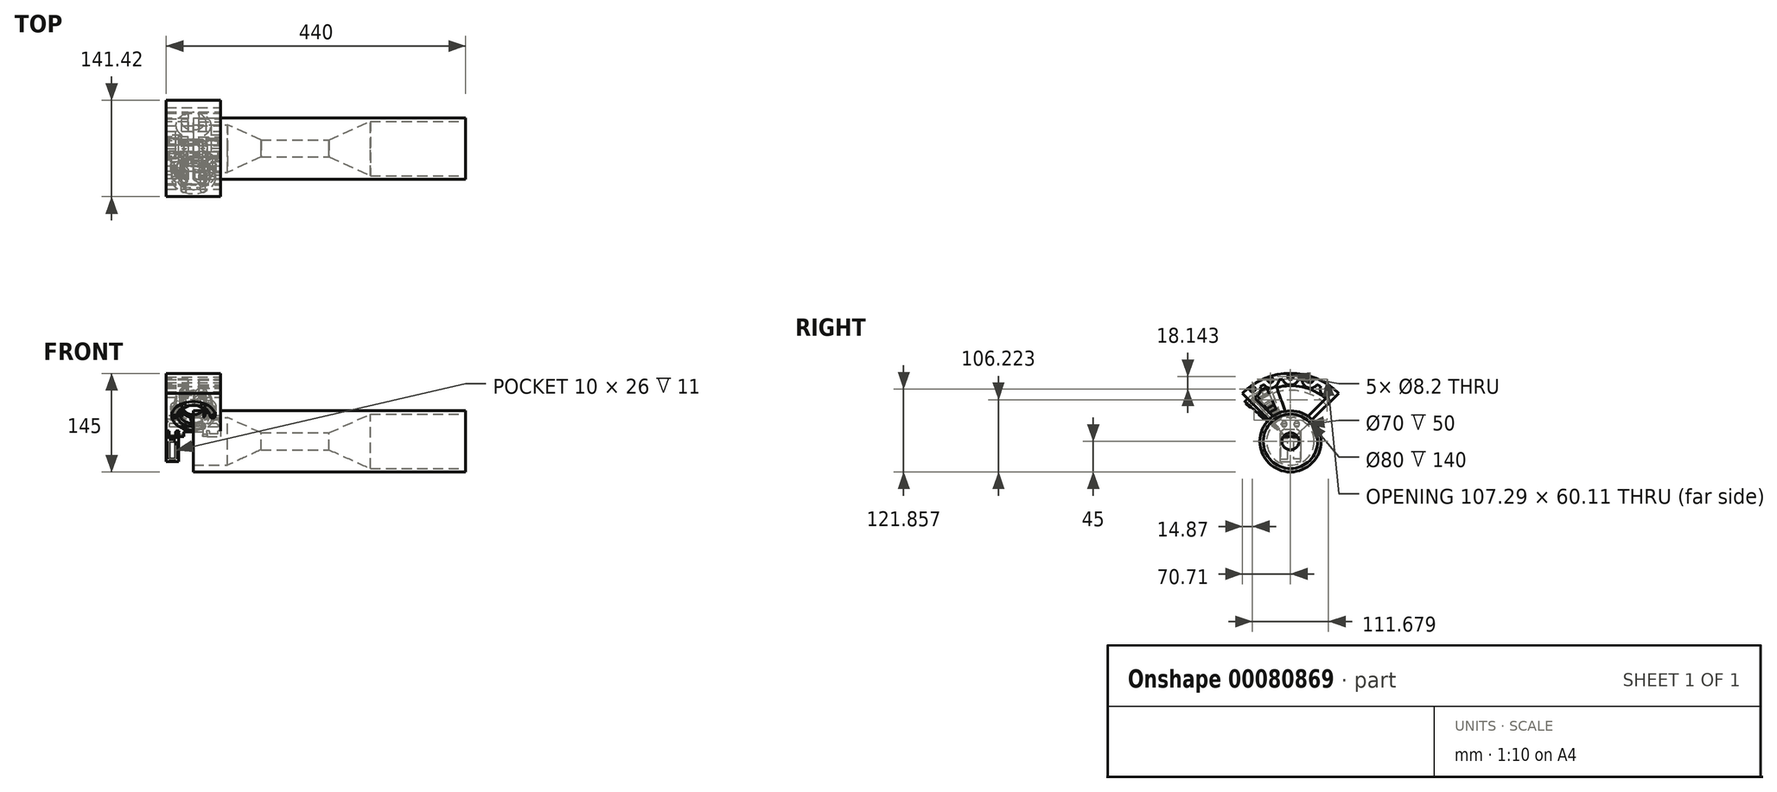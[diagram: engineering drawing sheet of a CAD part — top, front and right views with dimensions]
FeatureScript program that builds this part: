
annotation { "Feature Type Name" : "Feature", "Feature Type Description" : "" }
export const myFeature = defineFeature(function(context is Context, id is Id, definition is map)
    precondition{}
    {
        {
            var Q0;
            Q0=qCreatedBy(makeId("Front.planeOp"),FACE);
            var sketch = newSketch(context, id + "F0", { "sketchPlane" : qUnion([Q0])});
            skLineSegment(sketch, "E0.bottom", {"start": v(-40, 30) * mm, "end": v(40, 30) * mm});
            skLineSegment(sketch, "E0.top", {"start": v(-40, -30) * mm, "end": v(40, -30) * mm});
            skLineSegment(sketch, "E0.left", {"start": v(-40, 30) * mm, "end": v(-40, -30) * mm});
            skLineSegment(sketch, "E0.right", {"start": v(40, 30) * mm, "end": v(40, -30) * mm});
            skPoint(sketch, "E0.middle", {"position": v(0, 0) * mm});
            skLineSegment(sketch, "E1", {"start": v(-22, -30) * mm, "end": v(-22, 18) * mm});
            skLineSegment(sketch, "E2", {"start": v(-22, 18) * mm, "end": v(20, 18) * mm});
            skLineSegment(sketch, "E3", {"start": v(20, 18) * mm, "end": v(20, 7) * mm});
            skLineSegment(sketch, "E4", {"start": v(20, 7) * mm, "end": v(40, 7) * mm});
            skSolve(sketch);
        }
        {
            var Q0;
            {var subQ1=sQuery(id+"F0.wireOp",EDGE,"E0.bottom");Q0=makeQuery(id+"F0.imprint","IMPRINT",FACE,{"disambiguationData":[TD([[makeQuery(id+"F0.imprint","IMPRINT",EDGE,{"derivedFrom":subQ1}),-1.0]])]});}
            extrude(context, id + "F1", {"entities" : qUnion([Q0]), "depth" : 15 * mm});
        }
        {
            var Q0;
            Q0=makeQuery(id+"F1.opExtrude","SWEPT_EDGE",EDGE,{"disambiguationData":[OSD([sQuery(id+"F0.wireOp",EDGE,"E1"),sQuery(id+"F0.wireOp",EDGE,"E2")])]});
            var Q1;
            Q1=makeQuery(id+"F1.opExtrude","SWEPT_EDGE",EDGE,{"disambiguationData":[OSD([sQuery(id+"F0.wireOp",EDGE,"E2"),sQuery(id+"F0.wireOp",EDGE,"E3")])]});
            var Q2;
            Q2=makeQuery(id+"F1.opExtrude","SWEPT_EDGE",EDGE,{"disambiguationData":[OSD([sQuery(id+"F0.wireOp",EDGE,"E0.bottom"),sQuery(id+"F0.wireOp",EDGE,"E0.right")])]});
            var Q3;
            Q3=makeQuery(id+"F1.opExtrude","SWEPT_EDGE",EDGE,{"disambiguationData":[OSD([sQuery(id+"F0.wireOp",EDGE,"E0.bottom"),sQuery(id+"F0.wireOp",EDGE,"E0.left")])]});
            fillet(context, id + "F2", {"entities" : qUnion([Q0, Q1, Q2, Q3]), "radius" : 6 * mm, "tangentPropagation" : true, "allowEdgeOverflow" : false});
        }
        {
            var Q0;
            Q0=makeQuery(id+"F1.opExtrude","CAP_FACE",FACE,{"disambiguationData":[OSD([sQuery(id+"F0.wireOp",EDGE,"E0.bottom"),sQuery(id+"F0.wireOp",EDGE,"E0.top"),sQuery(id+"F0.wireOp",EDGE,"E0.left"),sQuery(id+"F0.wireOp",EDGE,"E0.right"),sQuery(id+"F0.wireOp",EDGE,"E1"),sQuery(id+"F0.wireOp",EDGE,"E2"),sQuery(id+"F0.wireOp",EDGE,"E3"),sQuery(id+"F0.wireOp",EDGE,"E4")])],"isStart":false});
            shell(context, id + "F3", {"entities" : qUnion([Q0]), "thickness" : 4 * mm});
        }
        {
            var Q0;
            Q0=qCreatedBy(makeId("Front.planeOp"),FACE);
            var sketch = newSketch(context, id + "F4", { "sketchPlane" : qUnion([Q0])});
            skLineSegment(sketch, "E5.bottom", {"start": v(-15, 18) * mm, "end": v(-11, 18) * mm});
            skLineSegment(sketch, "E5.top", {"start": v(-15, 30) * mm, "end": v(-11, 30) * mm});
            skLineSegment(sketch, "E5.left", {"start": v(-15, 18) * mm, "end": v(-15, 30) * mm});
            skLineSegment(sketch, "E5.right", {"start": v(-11, 18) * mm, "end": v(-11, 30) * mm});
            skLineSegment(sketch, "E6.bottom", {"start": v(13, 18) * mm, "end": v(9, 18) * mm});
            skLineSegment(sketch, "E6.top", {"start": v(13, 30) * mm, "end": v(9, 30) * mm});
            skLineSegment(sketch, "E6.left", {"start": v(13, 18) * mm, "end": v(13, 30) * mm});
            skLineSegment(sketch, "E6.right", {"start": v(9, 18) * mm, "end": v(9, 30) * mm});
            skLineSegment(sketch, "E7.bottom", {"start": v(-22, 4) * mm, "end": v(-40, 4) * mm});
            skLineSegment(sketch, "E7.top", {"start": v(-22, 0) * mm, "end": v(-40, 0) * mm});
            skLineSegment(sketch, "E7.left", {"start": v(-22, 4) * mm, "end": v(-22, 0) * mm});
            skLineSegment(sketch, "E7.right", {"start": v(-40, 4) * mm, "end": v(-40, 0) * mm});
            skSolve(sketch);
        }
        {
            var Q0;
            Q0 = qSketchRegion(id + "F4", true);
            var Q1;
            Q1=makeQuery(id+"F1.opExtrude","CAP_FACE",FACE,{"disambiguationData":[OSD([sQuery(id+"F0.wireOp",EDGE,"E0.bottom"),sQuery(id+"F0.wireOp",EDGE,"E0.top"),sQuery(id+"F0.wireOp",EDGE,"E0.left"),sQuery(id+"F0.wireOp",EDGE,"E0.right"),sQuery(id+"F0.wireOp",EDGE,"E1"),sQuery(id+"F0.wireOp",EDGE,"E2"),sQuery(id+"F0.wireOp",EDGE,"E3"),sQuery(id+"F0.wireOp",EDGE,"E4")])],"isStart":false});
            extrude(context, id + "F5", {"entities" : qUnion([Q0]), "operationType" : NewBodyOperationType.ADD, "endBound" : BoundingType.UP_TO_SURFACE, "endBoundEntityFace" : qUnion([Q1]), "depth" : 25 * mm});
        }
        {
            var Q0;
            Q0=qCreatedBy(makeId("Front.planeOp"),FACE);
            var sketch = newSketch(context, id + "F6", { "sketchPlane" : qUnion([Q0])});
            skCircle(sketch, "E8", {"center": v(0, 57) * mm, "radius": 18 * mm});
            skLineSegment(sketch, "E9", {"start": v(0, 57) * mm, "end": v(0, 75) * mm, "construction": true});
            skLineSegment(sketch, "E10", {"start": v(0, 75) * mm, "end": v(0, 100) * mm});
            skLineSegment(sketch, "E11", {"start": v(0, 100) * mm, "end": v(-40, 100) * mm});
            skLineSegment(sketch, "E12", {"start": v(-40, 100) * mm, "end": v(-40, 10) * mm});
            skLineSegment(sketch, "E13", {"start": v(-40, 10) * mm, "end": v(0, 10) * mm});
            skLineSegment(sketch, "E14", {"start": v(0, 10) * mm, "end": v(0, 39) * mm});
            skCircle(sketch, "E15", {"center": v(0, 57) * mm, "radius": 21 * mm});
            skLineSegment(sketch, "E16", {"start": v(0, 57) * mm, "end": v(0, 78) * mm, "construction": true});
            skLineSegment(sketch, "E17", {"start": v(-14, 20) * mm, "end": v(-14, 10) * mm});
            skLineSegment(sketch, "E18", {"start": v(0, 100) * mm, "end": v(40, 100) * mm});
            skLineSegment(sketch, "E19", {"start": v(40, 100) * mm, "end": v(40, 10) * mm});
            skLineSegment(sketch, "E20", {"start": v(40, 10) * mm, "end": v(0, 10) * mm});
            skLineSegment(sketch, "E21", {"start": v(14, 20) * mm, "end": v(14, 10) * mm});
            skLineSegment(sketch, "E22", {"start": v(-14, 20) * mm, "end": v(0, 20) * mm});
            skLineSegment(sketch, "E23", {"start": v(0, 20) * mm, "end": v(14, 20) * mm});
            skLineSegment(sketch, "E24", {"start": v(-73.82, 0) * mm, "end": v(0, 0) * mm, "construction": true});
            skLineSegment(sketch, "E25", {"start": v(-7, 20) * mm, "end": v(-7, 69.12) * mm});
            skLineSegment(sketch, "E26", {"start": v(7, 69.12) * mm, "end": v(7, 20) * mm});
            skArc(sketch, "E27", {"start": v(-7, 44.88) * mm, "mid": v(0, 43) * mm, "end": v(7, 44.88) * mm});
            skArc(sketch, "E28.trimOffspring", {"start": v(7, 69.12) * mm, "mid": v(0, 71) * mm, "end": v(-7, 69.12) * mm});
            skSolve(sketch);
        }
        {
            var Q0;
            Q0=qCreatedBy(makeId("Front.planeOp"),FACE);
            var sketch = newSketch(context, id + "F7", { "sketchPlane" : qUnion([Q0])});
            skCircle(sketch, "E29", {"center": v(0, 57) * mm, "radius": 17.5 * mm});
            skFitSpline(sketch, "E30", {"points": [v(30.32, 90.11) * mm, v(16.42, 89.95) * mm, v(3.9, 90.3) * mm, v(-9.37, 84.06) * mm, v(-14.84, 66.27) * mm], "startDerivative": vector(-71.71, -0.04) * mm, "endDerivative": vector(12.52, -60.5) * mm});
            skLineSegment(sketch, "E31", {"start": v(30.32, 90.11) * mm, "end": v(30.32, 54.44) * mm});
            skFitSpline(sketch, "E32", {"points": [v(30.32, 84.61) * mm, v(15.77, 85.1) * mm, v(3.67, 86.27) * mm, v(-7.6, 81.73) * mm, v(-12.16, 69.59) * mm], "startDerivative": vector(-60.22, -2.48) * mm, "endDerivative": vector(5.72, -55.41) * mm});
            skLineSegment(sketch, "E33", {"start": v(-14.84, 66.27) * mm, "end": v(0, 57) * mm});
            skLineSegment(sketch, "E34", {"start": v(-12.16, 69.59) * mm, "end": v(0, 57) * mm});
            skLineSegment(sketch, "E35", {"start": v(0, 57) * mm, "end": v(12.68, 57) * mm, "construction": true});
            skLineSegment(sketch, "E36", {"start": v(-9.27, 71.84) * mm, "end": v(0, 57) * mm});
            skLineSegment(sketch, "E37", {"start": v(-5.99, 73.44) * mm, "end": v(0, 57) * mm});
            skFitSpline(sketch, "E38", {"points": [v(-9.27, 71.84) * mm, v(-6.14, 79.83) * mm, v(3.5, 83.27) * mm, v(15.33, 81.84) * mm, v(30.32, 79.91) * mm], "startDerivative": vector(-7.84, 49.59) * mm, "endDerivative": vector(53.8, -1.16) * mm});
            skFitSpline(sketch, "E39", {"points": [v(-5.99, 73.44) * mm, v(-4.56, 77.76) * mm, v(3.32, 80.07) * mm, v(14.76, 77.58) * mm, v(30.32, 74.41) * mm], "startDerivative": vector(-8.8, 35.89) * mm, "endDerivative": vector(51.1, -3.45) * mm});
            skLineSegment(sketch, "E40", {"start": v(-9.37, 84.06) * mm, "end": v(-4.56, 77.76) * mm, "construction": true});
            skLineSegment(sketch, "E41", {"start": v(3.9, 90.3) * mm, "end": v(3.32, 80.07) * mm, "construction": true});
            skLineSegment(sketch, "E42", {"start": v(16.42, 89.95) * mm, "end": v(14.76, 77.58) * mm, "construction": true});
            skSolve(sketch);
        }
        {
            var Q0;
            {var subQ0=sQuery(id+"F6.wireOp",EDGE,"E18");Q0=makeQuery(id+"F6.imprint","IMPRINT",FACE,{"disambiguationData":[TD([[makeQuery(id+"F6.imprint","IMPRINT",EDGE,{"derivedFrom":subQ0}),-1.0]])]});}
            var Q1;
            {var subQ1=sQuery(id+"F6.wireOp",EDGE,"E14");var subQ3=sQuery(id+"F6.wireOp",EDGE,"E15");var subQ4=makeQuery(id+"F6.imprint","INTERSECT",VERTEX,{"derivedFrom":[subQ1,subQ3]});Q1=makeQuery(id+"F6.imprint","IMPRINT",FACE,{"disambiguationData":[TD([[makeQuery(id+"F6.imprint","IMPRINT",EDGE,{"disambiguationData":[TD([[subQ4,-1.0]])],"derivedFrom":subQ3}),-1.0]])]});}
            var Q2;
            {var subQ0=sQuery(id+"F6.wireOp",EDGE,"E14");var subQ1=sQuery(id+"F6.wireOp",EDGE,"E8");var subQ2=makeQuery(id+"F6.imprint","INTERSECT",VERTEX,{"derivedFrom":[subQ1,subQ0]});Q2=makeQuery(id+"F6.imprint","IMPRINT",FACE,{"disambiguationData":[TD([[makeQuery(id+"F6.imprint","IMPRINT",EDGE,{"disambiguationData":[TD([[subQ2,-1.0]])],"derivedFrom":subQ1}),-1.0]])]});}
            var Q3;
            {var subQ0=sQuery(id+"F6.wireOp",EDGE,"E10");var subQ1=sQuery(id+"F6.wireOp",EDGE,"E8");var subQ2=makeQuery(id+"F6.imprint","INTERSECT",VERTEX,{"derivedFrom":[subQ1,subQ0]});Q3=makeQuery(id+"F6.imprint","IMPRINT",FACE,{"disambiguationData":[TD([[makeQuery(id+"F6.imprint","IMPRINT",EDGE,{"disambiguationData":[TD([[subQ2,1.0]])],"derivedFrom":subQ1}),-1.0]])]});}
            var Q4;
            Q4=sQuery(id+"F6.wireOp",EDGE,"E24");
            revolve(context, id + "F8", {"entities" : qUnion([Q0, Q1, Q2, Q3]), "axis" : qUnion([Q4]), "revolveType" : RevolveType.SYMMETRIC, "angle" : 90 * degree});
        }
        {
            var Q0;
            {var subQ0=sQuery(id+"F6.wireOp",EDGE,"E14");var subQ1=sQuery(id+"F6.wireOp",EDGE,"E8");var subQ2=makeQuery(id+"F6.imprint","INTERSECT",VERTEX,{"derivedFrom":[subQ1,subQ0]});Q0=makeQuery(id+"F6.imprint","IMPRINT",FACE,{"disambiguationData":[TD([[makeQuery(id+"F6.imprint","IMPRINT",EDGE,{"disambiguationData":[TD([[subQ2,1.0]])],"derivedFrom":subQ1}),-1.0]])]});}
            var Q1;
            {var subQ1=sQuery(id+"F6.wireOp",EDGE,"E14");var subQ3=sQuery(id+"F6.wireOp",EDGE,"E15");var subQ4=makeQuery(id+"F6.imprint","INTERSECT",VERTEX,{"derivedFrom":[subQ1,subQ3]});Q1=makeQuery(id+"F6.imprint","IMPRINT",FACE,{"disambiguationData":[TD([[makeQuery(id+"F6.imprint","IMPRINT",EDGE,{"disambiguationData":[TD([[subQ4,1.0]])],"derivedFrom":subQ3}),-1.0]])]});}
            var Q2;
            {var subQ10=sQuery(id+"F6.wireOp",EDGE,"E11");Q2=makeQuery(id+"F6.imprint","IMPRINT",FACE,{"disambiguationData":[TD([[makeQuery(id+"F6.imprint","IMPRINT",EDGE,{"derivedFrom":subQ10}),1.0]])]});}
            var Q3;
            {var subQ0=sQuery(id+"F6.wireOp",EDGE,"E10");var subQ1=sQuery(id+"F6.wireOp",EDGE,"E8");var subQ2=makeQuery(id+"F6.imprint","INTERSECT",VERTEX,{"derivedFrom":[subQ1,subQ0]});Q3=makeQuery(id+"F6.imprint","IMPRINT",FACE,{"disambiguationData":[TD([[makeQuery(id+"F6.imprint","IMPRINT",EDGE,{"disambiguationData":[TD([[subQ2,-1.0]])],"derivedFrom":subQ1}),-1.0]])]});}
            var Q4;
            Q4=sQuery(id+"F6.wireOp",EDGE,"E24");
            revolve(context, id + "F9", {"entities" : qUnion([Q0, Q1, Q2, Q3]), "axis" : qUnion([Q4]), "revolveType" : RevolveType.SYMMETRIC, "angle" : 90 * degree});
        }
        {
            var Q0;
            {var subQ0=sQuery(id+"F6.wireOp",EDGE,"E14");var subQ1=sQuery(id+"F6.wireOp",EDGE,"E10");var subQ2=sQuery(id+"F6.wireOp",EDGE,"E8");Q0=makeQuery(id+"FP5FcsPlQxCtVq2_5.opBoolean","MERGE",FACE,{"derivedFrom":[makeQuery(id+"F8.opRevolve","CAP_FACE",FACE,{"disambiguationData":[OSD([subQ2,subQ1,subQ0,sQuery(id+"F6.wireOp",EDGE,"E18"),sQuery(id+"F6.wireOp",EDGE,"E19"),sQuery(id+"F6.wireOp",EDGE,"E20"),sQuery(id+"F6.wireOp",EDGE,"E21"),sQuery(id+"F6.wireOp",EDGE,"E23")])],"isStart":false}),makeQuery(id+"F9.opRevolve","CAP_FACE",FACE,{"disambiguationData":[OSD([subQ2,subQ1,sQuery(id+"F6.wireOp",EDGE,"E11"),sQuery(id+"F6.wireOp",EDGE,"E12"),sQuery(id+"F6.wireOp",EDGE,"E13"),subQ0,sQuery(id+"F6.wireOp",EDGE,"E17"),sQuery(id+"F6.wireOp",EDGE,"E22")])],"isStart":false})]});}
            var sketch = newSketch(context, id + "F10", { "sketchPlane" : qUnion([Q0])});
            skCircle(sketch, "E43.0", {"center": v(0, 57) * mm, "radius": 18 * mm});
            skCircle(sketch, "E44", {"center": v(0, 57) * mm, "radius": 20 * mm});
            skSolve(sketch);
        }
        {
            var Q0;
            Q0=makeQuery(id+"F10.imprint","IMPRINT",FACE,{"disambiguationData":[TD([[makeQuery(id+"F10.imprint","IMPRINT",EDGE,{"derivedFrom":sQuery(id+"F10.wireOp",EDGE,"E43.0")}),-1.0]])]});
            var Q1;
            Q1=makeQuery(id+"F10.imprint","IMPRINT",FACE,{"disambiguationData":[TD([[makeQuery(id+"F10.imprint","IMPRINT",EDGE,{"derivedFrom":sQuery(id+"F10.wireOp",EDGE,"E43.0")}),1.0]])]});
            var Q2;
            Q2=sQuery(id+"F6.wireOp",EDGE,"E24");
            revolve(context, id + "F11", {"operationType" : NewBodyOperationType.REMOVE, "entities" : qUnion([Q0, Q1]), "axis" : qUnion([Q2]), "revolveType" : RevolveType.ONE_DIRECTION, "oppositeDirection" : true, "angle" : 25 * degree});
        }
        {
            var Q0;
            {var subQ0=sQuery(id+"F6.wireOp",EDGE,"E14");var subQ1=sQuery(id+"F6.wireOp",EDGE,"E10");var subQ2=sQuery(id+"F6.wireOp",EDGE,"E8");Q0=makeQuery(id+"FP5FcsPlQxCtVq2_5.opBoolean","MERGE",FACE,{"derivedFrom":[makeQuery(id+"F8.opRevolve","CAP_FACE",FACE,{"disambiguationData":[OSD([subQ2,subQ1,subQ0,sQuery(id+"F6.wireOp",EDGE,"E18"),sQuery(id+"F6.wireOp",EDGE,"E19"),sQuery(id+"F6.wireOp",EDGE,"E20"),sQuery(id+"F6.wireOp",EDGE,"E21"),sQuery(id+"F6.wireOp",EDGE,"E23")])],"isStart":true}),makeQuery(id+"F9.opRevolve","CAP_FACE",FACE,{"disambiguationData":[OSD([subQ2,subQ1,sQuery(id+"F6.wireOp",EDGE,"E11"),sQuery(id+"F6.wireOp",EDGE,"E12"),sQuery(id+"F6.wireOp",EDGE,"E13"),subQ0,sQuery(id+"F6.wireOp",EDGE,"E17"),sQuery(id+"F6.wireOp",EDGE,"E22")])],"isStart":true})]});}
            var sketch = newSketch(context, id + "F12", { "sketchPlane" : qUnion([Q0])});
            skCircle(sketch, "E45.0", {"center": v(0, -57) * mm, "radius": 18 * mm});
            skCircle(sketch, "E46", {"center": v(0, -57) * mm, "radius": 20.4 * mm});
            skSolve(sketch);
        }
        {
            var Q0;
            Q0=makeQuery(id+"F12.imprint","IMPRINT",FACE,{"disambiguationData":[TD([[makeQuery(id+"F12.imprint","IMPRINT",EDGE,{"derivedFrom":sQuery(id+"F12.wireOp",EDGE,"E45.0")}),-1.0]])]});
            var Q1;
            Q1=makeQuery(id+"F12.imprint","IMPRINT",FACE,{"disambiguationData":[TD([[makeQuery(id+"F12.imprint","IMPRINT",EDGE,{"derivedFrom":sQuery(id+"F12.wireOp",EDGE,"E45.0")}),1.0]])]});
            var Q2;
            Q2=sQuery(id+"F6.wireOp",EDGE,"E24");
            revolve(context, id + "F13", {"operationType" : NewBodyOperationType.REMOVE, "entities" : qUnion([Q0, Q1]), "axis" : qUnion([Q2]), "revolveType" : RevolveType.ONE_DIRECTION, "angle" : 10 * degree});
        }
        {
            var Q0;
            Q0=makeQuery(id+"F9.opRevolve","SWEPT_FACE",FACE,{"disambiguationData":[OSD([sQuery(id+"F6.wireOp",EDGE,"E12")])]});
            var sketch = newSketch(context, id + "F14", { "sketchPlane" : qUnion([Q0])});
            skCircle(sketch, "E47", {"center": v(-32.78, 55.43) * mm, "radius": 2.65 * mm});
            skSolve(sketch);
        }
        {
            var Q0;
            Q0=qCreatedBy(makeId("Front.planeOp"),FACE);
            var sketch = newSketch(context, id + "F15", { "sketchPlane" : qUnion([Q0])});
            skLineSegment(sketch, "E48", {"start": v(0, 0) * mm, "end": v(76.53, 0) * mm, "construction": true});
            skLineSegment(sketch, "E49", {"start": v(0, 0) * mm, "end": v(44.43, 25.65) * mm, "construction": true});
            skLineSegment(sketch, "E50", {"start": v(14.78, 10.27) * mm, "end": v(26.3, 8.24) * mm});
            skArc(sketch, "E51", {"start": v(24.05, 2.63) * mm, "mid": v(23.32, 3.46) * mm, "end": v(22.43, 4.12) * mm});
            skLineSegment(sketch, "E52", {"start": v(22.43, 4.12) * mm, "end": v(16.28, 7.67) * mm});
            skArc(sketch, "E53", {"start": v(24.05, 2.63) * mm, "mid": v(27.79, -4.97) * mm, "end": v(33, 1.71) * mm});
            skLineSegment(sketch, "E54", {"start": v(28.3, 0) * mm, "end": v(0, 0) * mm, "construction": true});
            skArc(sketch, "E55.trimOffspring", {"start": v(16.28, 7.67) * mm, "mid": v(15.59, 9) * mm, "end": v(14.78, 10.27) * mm});
            skLineSegment(sketch, "E56", {"start": v(14.78, 10.27) * mm, "end": v(16.28, 7.67) * mm});
            skPoint(sketch, "E57", {"position": v(15.53, 8.97) * mm});
            skLineSegment(sketch, "E58", {"start": v(28.3, 0) * mm, "end": v(33, 1.71) * mm, "construction": true});
            skArc(sketch, "E59", {"start": v(33, 1.71) * mm, "mid": v(30.66, 6) * mm, "end": v(26.3, 8.24) * mm});
            skLineSegment(sketch, "E60", {"start": v(0, 0) * mm, "end": v(0, 28.5) * mm});
            skLineSegment(sketch, "E61.1.0", {"start": v(7.65, 21.49) * mm, "end": v(1.5, 17.94) * mm});
            skLineSegment(sketch, "E61.1.1", {"start": v(14.15, 24.5) * mm, "end": v(15.02, 29.43) * mm, "construction": true});
            skArc(sketch, "E61.1.2", {"start": v(15.02, 29.43) * mm, "mid": v(10.13, 29.55) * mm, "end": v(6.02, 26.9) * mm});
            skPoint(sketch, "E61.1.3", {"position": v(0, 17.94) * mm});
            skArc(sketch, "E61.1.4", {"start": v(9.75, 22.14) * mm, "mid": v(18.2, 21.58) * mm, "end": v(15.02, 29.43) * mm});
            skLineSegment(sketch, "E61.1.5", {"start": v(-1.5, 17.94) * mm, "end": v(6.02, 26.9) * mm});
            skArc(sketch, "E61.1.6", {"start": v(1.5, 17.94) * mm, "mid": v(0, 18) * mm, "end": v(-1.5, 17.94) * mm});
            skArc(sketch, "E61.1.7", {"start": v(9.75, 22.14) * mm, "mid": v(8.66, 21.93) * mm, "end": v(7.65, 21.49) * mm});
            skLineSegment(sketch, "E61.1.8", {"start": v(-1.5, 17.94) * mm, "end": v(1.5, 17.94) * mm});
            skLineSegment(sketch, "E61.2.0", {"start": v(-14.78, 17.37) * mm, "end": v(-14.78, 10.27) * mm});
            skLineSegment(sketch, "E61.2.1", {"start": v(-14.15, 24.5) * mm, "end": v(-17.98, 27.72) * mm, "construction": true});
            skArc(sketch, "E61.2.2", {"start": v(-17.98, 27.72) * mm, "mid": v(-20.53, 23.55) * mm, "end": v(-20.29, 18.66) * mm});
            skPoint(sketch, "E61.2.3", {"position": v(-15.53, 8.97) * mm});
            skArc(sketch, "E61.2.4", {"start": v(-14.3, 19.51) * mm, "mid": v(-9.59, 26.55) * mm, "end": v(-17.98, 27.72) * mm});
            skLineSegment(sketch, "E61.2.5", {"start": v(-16.28, 7.67) * mm, "end": v(-20.29, 18.66) * mm});
            skArc(sketch, "E61.2.6", {"start": v(-14.78, 10.27) * mm, "mid": v(-15.59, 9) * mm, "end": v(-16.28, 7.67) * mm});
            skArc(sketch, "E61.2.7", {"start": v(-14.3, 19.51) * mm, "mid": v(-14.66, 18.47) * mm, "end": v(-14.78, 17.37) * mm});
            skLineSegment(sketch, "E61.2.8", {"start": v(-16.28, 7.67) * mm, "end": v(-14.78, 10.27) * mm});
            skLineSegment(sketch, "E62.2.3.0", {"start": v(-22.43, -4.12) * mm, "end": v(-16.28, -7.67) * mm});
            skLineSegment(sketch, "E62.3.3.0", {"start": v(-28.3, 0) * mm, "end": v(-33, -1.71) * mm, "construction": true});
            skArc(sketch, "E62.6.3.0", {"start": v(-33, -1.71) * mm, "mid": v(-30.66, -6) * mm, "end": v(-26.3, -8.24) * mm});
            skPoint(sketch, "E62.10.3.0", {"position": v(-15.53, -8.97) * mm});
            skArc(sketch, "E62.11.3.0", {"start": v(-24.05, -2.63) * mm, "mid": v(-27.79, 4.97) * mm, "end": v(-33, -1.71) * mm});
            skLineSegment(sketch, "E62.15.3.0", {"start": v(-14.78, -10.27) * mm, "end": v(-26.3, -8.24) * mm});
            skArc(sketch, "E62.18.3.0", {"start": v(-16.28, -7.67) * mm, "mid": v(-15.59, -9) * mm, "end": v(-14.78, -10.27) * mm});
            skArc(sketch, "E62.22.3.0", {"start": v(-24.05, -2.63) * mm, "mid": v(-23.32, -3.46) * mm, "end": v(-22.43, -4.12) * mm});
            skLineSegment(sketch, "E62.26.3.0", {"start": v(-14.78, -10.27) * mm, "end": v(-16.28, -7.67) * mm});
            skLineSegment(sketch, "E63.2.4.0", {"start": v(-7.65, -21.49) * mm, "end": v(-1.5, -17.94) * mm});
            skLineSegment(sketch, "E63.3.4.0", {"start": v(-14.15, -24.5) * mm, "end": v(-15.02, -29.43) * mm, "construction": true});
            skArc(sketch, "E63.6.4.0", {"start": v(-15.02, -29.43) * mm, "mid": v(-10.13, -29.55) * mm, "end": v(-6.02, -26.9) * mm});
            skPoint(sketch, "E63.10.4.0", {"position": v(0, -17.94) * mm});
            skArc(sketch, "E63.11.4.0", {"start": v(-9.75, -22.14) * mm, "mid": v(-18.2, -21.58) * mm, "end": v(-15.02, -29.43) * mm});
            skLineSegment(sketch, "E63.15.4.0", {"start": v(1.5, -17.94) * mm, "end": v(-6.02, -26.9) * mm});
            skArc(sketch, "E63.18.4.0", {"start": v(-1.5, -17.94) * mm, "mid": v(0, -18) * mm, "end": v(1.5, -17.94) * mm});
            skArc(sketch, "E63.22.4.0", {"start": v(-9.75, -22.14) * mm, "mid": v(-8.66, -21.93) * mm, "end": v(-7.65, -21.49) * mm});
            skLineSegment(sketch, "E63.26.4.0", {"start": v(1.5, -17.94) * mm, "end": v(-1.5, -17.94) * mm});
            skLineSegment(sketch, "E63.2.5.0", {"start": v(14.78, -17.37) * mm, "end": v(14.78, -10.27) * mm});
            skLineSegment(sketch, "E63.3.5.0", {"start": v(14.15, -24.5) * mm, "end": v(17.98, -27.72) * mm, "construction": true});
            skArc(sketch, "E63.6.5.0", {"start": v(17.98, -27.72) * mm, "mid": v(20.53, -23.55) * mm, "end": v(20.29, -18.66) * mm});
            skPoint(sketch, "E63.10.5.0", {"position": v(15.53, -8.97) * mm});
            skArc(sketch, "E63.11.5.0", {"start": v(14.3, -19.51) * mm, "mid": v(9.59, -26.55) * mm, "end": v(17.98, -27.72) * mm});
            skLineSegment(sketch, "E63.15.5.0", {"start": v(16.28, -7.67) * mm, "end": v(20.29, -18.66) * mm});
            skArc(sketch, "E63.18.5.0", {"start": v(14.78, -10.27) * mm, "mid": v(15.59, -9) * mm, "end": v(16.28, -7.67) * mm});
            skArc(sketch, "E63.22.5.0", {"start": v(14.3, -19.51) * mm, "mid": v(14.66, -18.47) * mm, "end": v(14.78, -17.37) * mm});
            skLineSegment(sketch, "E63.26.5.0", {"start": v(16.28, -7.67) * mm, "end": v(14.78, -10.27) * mm});
            skLineSegment(sketch, "E64", {"start": v(0, 28.5) * mm, "end": v(-43.76, 28.5) * mm});
            skLineSegment(sketch, "E65", {"start": v(0, 0) * mm, "end": v(0, -57) * mm});
            skLineSegment(sketch, "E66", {"start": v(0, -57) * mm, "end": v(-24.38, -57) * mm});
            skSolve(sketch);
        }
        {
            var Q0;
            Q0=makeQuery(id+"F15.imprint","IMPRINT",FACE,{"disambiguationData":[TD([[makeQuery(id+"F15.imprint","IMPRINT",EDGE,{"derivedFrom":sQuery(id+"F15.wireOp",EDGE,"E63.2.5.0")}),-1.0]])]});
            var Q1;
            Q1=makeQuery(id+"F15.imprint","IMPRINT",FACE,{"disambiguationData":[TD([[makeQuery(id+"F15.imprint","IMPRINT",EDGE,{"derivedFrom":sQuery(id+"F15.wireOp",EDGE,"E50")}),-1.0]])]});
            var Q2;
            {var subQ1=sQuery(id+"F15.wireOp",EDGE,"E61.1.0");Q2=makeQuery(id+"F15.imprint","IMPRINT",FACE,{"disambiguationData":[TD([[makeQuery(id+"F15.imprint","IMPRINT",EDGE,{"derivedFrom":subQ1}),-1.0]])]});}
            var Q3;
            Q3=makeQuery(id+"F15.imprint","IMPRINT",FACE,{"disambiguationData":[TD([[makeQuery(id+"F15.imprint","IMPRINT",EDGE,{"derivedFrom":sQuery(id+"F15.wireOp",EDGE,"E61.2.0")}),-1.0]])]});
            var Q4;
            Q4=makeQuery(id+"F15.imprint","IMPRINT",FACE,{"disambiguationData":[TD([[makeQuery(id+"F15.imprint","IMPRINT",EDGE,{"derivedFrom":sQuery(id+"F15.wireOp",EDGE,"E62.2.3.0")}),-1.0]])]});
            var Q5;
            {var subQ4=sQuery(id+"F15.wireOp",EDGE,"E63.2.4.0");Q5=makeQuery(id+"F15.imprint","IMPRINT",FACE,{"disambiguationData":[TD([[makeQuery(id+"F15.imprint","IMPRINT",EDGE,{"derivedFrom":subQ4}),-1.0]])]});}
            var Q6;
            Q6=sQuery(id+"F15.wireOp",EDGE,"E66");
            revolve(context, id + "F16", {"entities" : qUnion([Q0, Q1, Q2, Q3, Q4, Q5]), "axis" : qUnion([Q6]), "revolveType" : RevolveType.SYMMETRIC, "angle" : 12 * degree});
        }
        {
            var Q0;
            Q0=makeQuery(id+"F16.opRevolve","SWEPT_BODY",BODY,{"disambiguationData":[OSD([sQuery(id+"F15.wireOp",EDGE,"E62.2.3.0"),sQuery(id+"F15.wireOp",EDGE,"E62.6.3.0"),sQuery(id+"F15.wireOp",EDGE,"E62.11.3.0"),sQuery(id+"F15.wireOp",EDGE,"E62.15.3.0"),sQuery(id+"F15.wireOp",EDGE,"E62.18.3.0"),sQuery(id+"F15.wireOp",EDGE,"E62.22.3.0")])]});
            var Q1;
            Q1=makeQuery(id+"F16.opRevolve","SWEPT_BODY",BODY,{"disambiguationData":[OSD([sQuery(id+"F15.wireOp",EDGE,"E61.2.0"),sQuery(id+"F15.wireOp",EDGE,"E61.2.2"),sQuery(id+"F15.wireOp",EDGE,"E61.2.4"),sQuery(id+"F15.wireOp",EDGE,"E61.2.5"),sQuery(id+"F15.wireOp",EDGE,"E61.2.6"),sQuery(id+"F15.wireOp",EDGE,"E61.2.7"),sQuery(id+"F15.wireOp",EDGE,"E64")])]});
            var Q2;
            Q2=makeQuery(id+"F16.opRevolve","SWEPT_BODY",BODY,{"disambiguationData":[OSD([sQuery(id+"F15.wireOp",EDGE,"E60"),sQuery(id+"F15.wireOp",EDGE,"E61.1.0"),sQuery(id+"F15.wireOp",EDGE,"E61.1.2"),sQuery(id+"F15.wireOp",EDGE,"E61.1.4"),sQuery(id+"F15.wireOp",EDGE,"E61.1.5"),sQuery(id+"F15.wireOp",EDGE,"E61.1.6"),sQuery(id+"F15.wireOp",EDGE,"E61.1.7")])]});
            var Q3;
            Q3=makeQuery(id+"F16.opRevolve","SWEPT_BODY",BODY,{"disambiguationData":[OSD([sQuery(id+"F15.wireOp",EDGE,"E50"),sQuery(id+"F15.wireOp",EDGE,"E51"),sQuery(id+"F15.wireOp",EDGE,"E52"),sQuery(id+"F15.wireOp",EDGE,"E53"),sQuery(id+"F15.wireOp",EDGE,"E55.trimOffspring"),sQuery(id+"F15.wireOp",EDGE,"E59")])]});
            var Q4;
            Q4=makeQuery(id+"F16.opRevolve","SWEPT_BODY",BODY,{"disambiguationData":[OSD([sQuery(id+"F15.wireOp",EDGE,"E63.2.4.0"),sQuery(id+"F15.wireOp",EDGE,"E63.6.4.0"),sQuery(id+"F15.wireOp",EDGE,"E63.11.4.0"),sQuery(id+"F15.wireOp",EDGE,"E63.15.4.0"),sQuery(id+"F15.wireOp",EDGE,"E63.18.4.0"),sQuery(id+"F15.wireOp",EDGE,"E63.22.4.0"),sQuery(id+"F15.wireOp",EDGE,"E65")])]});
            var Q5;
            Q5=makeQuery(id+"F16.opRevolve","SWEPT_BODY",BODY,{"disambiguationData":[OSD([sQuery(id+"F15.wireOp",EDGE,"E63.2.5.0"),sQuery(id+"F15.wireOp",EDGE,"E63.6.5.0"),sQuery(id+"F15.wireOp",EDGE,"E63.11.5.0"),sQuery(id+"F15.wireOp",EDGE,"E63.15.5.0"),sQuery(id+"F15.wireOp",EDGE,"E63.18.5.0"),sQuery(id+"F15.wireOp",EDGE,"E63.22.5.0")])]});
            transform(context, id + "F17", {"entities" : qUnion([Q0, Q1, Q2, Q3, Q4, Q5]), "transformType" : TransformType.TRANSLATION_3D, "dx" : 0 * mm, "dy" : 0 * mm, "dz" : 57 * mm, "makeCopy" : false});
        }
        {
            var Q0;
            Q0=qCreatedBy(makeId("Front.planeOp"),FACE);
            var sketch = newSketch(context, id + "F18", { "sketchPlane" : qUnion([Q0])});
            skCircle(sketch, "E67", {"center": v(-14.15, 32.31) * mm, "radius": 3.5 * mm});
            skCircle(sketch, "E68", {"center": v(-28.3, 56.69) * mm, "radius": 3.5 * mm});
            skCircle(sketch, "E69", {"center": v(14.15, 32.31) * mm, "radius": 3.5 * mm});
            skCircle(sketch, "E70", {"center": v(28.3, 56.69) * mm, "radius": 3.5 * mm});
            skCircle(sketch, "E71", {"center": v(14.15, 81.06) * mm, "radius": 3.5 * mm});
            skCircle(sketch, "E72", {"center": v(-14.15, 81.06) * mm, "radius": 3.5 * mm});
            skSolve(sketch);
        }
        {
            var Q0;
            Q0 = qSketchRegion(id + "F18", true);
            var Q1;
            Q1=sQuery(id+"F6.wireOp",EDGE,"E24");
            revolve(context, id + "F19", {"entities" : qUnion([Q0]), "axis" : qUnion([Q1]), "revolveType" : RevolveType.ONE_DIRECTION, "angle" : 20 * degree});
        }
        {
            var Q0;
            Q0=makeQuery(id+"F16.opRevolve","SWEPT_BODY",BODY,{"disambiguationData":[OSD([sQuery(id+"F15.wireOp",EDGE,"E62.2.3.0"),sQuery(id+"F15.wireOp",EDGE,"E62.6.3.0"),sQuery(id+"F15.wireOp",EDGE,"E62.11.3.0"),sQuery(id+"F15.wireOp",EDGE,"E62.15.3.0"),sQuery(id+"F15.wireOp",EDGE,"E62.18.3.0"),sQuery(id+"F15.wireOp",EDGE,"E62.22.3.0")])]});
            var Q1;
            Q1=makeQuery(id+"F16.opRevolve","SWEPT_BODY",BODY,{"disambiguationData":[OSD([sQuery(id+"F15.wireOp",EDGE,"E63.2.4.0"),sQuery(id+"F15.wireOp",EDGE,"E63.6.4.0"),sQuery(id+"F15.wireOp",EDGE,"E63.11.4.0"),sQuery(id+"F15.wireOp",EDGE,"E63.15.4.0"),sQuery(id+"F15.wireOp",EDGE,"E63.18.4.0"),sQuery(id+"F15.wireOp",EDGE,"E63.22.4.0"),sQuery(id+"F15.wireOp",EDGE,"E65")])]});
            var Q2;
            Q2=makeQuery(id+"F16.opRevolve","SWEPT_BODY",BODY,{"disambiguationData":[OSD([sQuery(id+"F15.wireOp",EDGE,"E63.2.5.0"),sQuery(id+"F15.wireOp",EDGE,"E63.6.5.0"),sQuery(id+"F15.wireOp",EDGE,"E63.11.5.0"),sQuery(id+"F15.wireOp",EDGE,"E63.15.5.0"),sQuery(id+"F15.wireOp",EDGE,"E63.18.5.0"),sQuery(id+"F15.wireOp",EDGE,"E63.22.5.0")])]});
            var Q3;
            Q3=makeQuery(id+"F16.opRevolve","SWEPT_BODY",BODY,{"disambiguationData":[OSD([sQuery(id+"F15.wireOp",EDGE,"E50"),sQuery(id+"F15.wireOp",EDGE,"E51"),sQuery(id+"F15.wireOp",EDGE,"E52"),sQuery(id+"F15.wireOp",EDGE,"E53"),sQuery(id+"F15.wireOp",EDGE,"E55.trimOffspring"),sQuery(id+"F15.wireOp",EDGE,"E59")])]});
            var Q4;
            Q4=makeQuery(id+"F16.opRevolve","SWEPT_BODY",BODY,{"disambiguationData":[OSD([sQuery(id+"F15.wireOp",EDGE,"E60"),sQuery(id+"F15.wireOp",EDGE,"E61.1.0"),sQuery(id+"F15.wireOp",EDGE,"E61.1.2"),sQuery(id+"F15.wireOp",EDGE,"E61.1.4"),sQuery(id+"F15.wireOp",EDGE,"E61.1.5"),sQuery(id+"F15.wireOp",EDGE,"E61.1.6"),sQuery(id+"F15.wireOp",EDGE,"E61.1.7")])]});
            var Q5;
            Q5=makeQuery(id+"F16.opRevolve","SWEPT_BODY",BODY,{"disambiguationData":[OSD([sQuery(id+"F15.wireOp",EDGE,"E61.2.0"),sQuery(id+"F15.wireOp",EDGE,"E61.2.2"),sQuery(id+"F15.wireOp",EDGE,"E61.2.4"),sQuery(id+"F15.wireOp",EDGE,"E61.2.5"),sQuery(id+"F15.wireOp",EDGE,"E61.2.6"),sQuery(id+"F15.wireOp",EDGE,"E61.2.7"),sQuery(id+"F15.wireOp",EDGE,"E64")])]});
            var Q6;
            Q6=makeQuery(id+"F19.opRevolve","SWEPT_BODY",BODY,{"disambiguationData":[OSD([sQuery(id+"F18.wireOp",EDGE,"E69")])]});
            var Q7;
            Q7=makeQuery(id+"F19.opRevolve","SWEPT_BODY",BODY,{"disambiguationData":[OSD([sQuery(id+"F18.wireOp",EDGE,"E70")])]});
            var Q8;
            Q8=makeQuery(id+"F19.opRevolve","SWEPT_BODY",BODY,{"disambiguationData":[OSD([sQuery(id+"F18.wireOp",EDGE,"E71")])]});
            var Q9;
            Q9=makeQuery(id+"F19.opRevolve","SWEPT_BODY",BODY,{"disambiguationData":[OSD([sQuery(id+"F18.wireOp",EDGE,"E67")])]});
            var Q10;
            Q10=makeQuery(id+"F19.opRevolve","SWEPT_BODY",BODY,{"disambiguationData":[OSD([sQuery(id+"F18.wireOp",EDGE,"E68")])]});
            var Q11;
            Q11=makeQuery(id+"F19.opRevolve","SWEPT_BODY",BODY,{"disambiguationData":[OSD([sQuery(id+"F18.wireOp",EDGE,"E72")])]});
            var Q12;
            Q12=sQuery(id+"F6.wireOp",EDGE,"E24");
            transform(context, id + "F20", {"entities" : qUnion([Q0, Q1, Q2, Q3, Q4, Q5, Q6, Q7, Q8, Q9, Q10, Q11]), "transformType" : TransformType.ROTATION, "transformAxis" : qUnion([Q12]), "angle" : 30 * degree, "makeCopy" : false});
        }
        {
            var Q0;
            {var subQ0=sQuery(id+"F6.wireOp",EDGE,"E14");var subQ1=sQuery(id+"F6.wireOp",EDGE,"E10");var subQ2=sQuery(id+"F6.wireOp",EDGE,"E8");Q0=makeQuery(id+"F11.boolean.opBoolean","MERGE",FACE,{"derivedFrom":[makeQuery(id+"FP5FcsPlQxCtVq2_5.opBoolean","MERGE",FACE,{"derivedFrom":[makeQuery(id+"F8.opRevolve","CAP_FACE",FACE,{"disambiguationData":[OSD([subQ2,subQ1,subQ0,sQuery(id+"F6.wireOp",EDGE,"E18"),sQuery(id+"F6.wireOp",EDGE,"E19"),sQuery(id+"F6.wireOp",EDGE,"E20"),sQuery(id+"F6.wireOp",EDGE,"E21"),sQuery(id+"F6.wireOp",EDGE,"E23")])],"isStart":false}),makeQuery(id+"F9.opRevolve","CAP_FACE",FACE,{"disambiguationData":[OSD([subQ2,subQ1,sQuery(id+"F6.wireOp",EDGE,"E11"),sQuery(id+"F6.wireOp",EDGE,"E12"),sQuery(id+"F6.wireOp",EDGE,"E13"),subQ0,sQuery(id+"F6.wireOp",EDGE,"E17"),sQuery(id+"F6.wireOp",EDGE,"E22")])],"isStart":false})]}),makeQuery(id+"F11.opRevolve","CAP_FACE",FACE,{"disambiguationData":[OSD([sQuery(id+"F10.wireOp",EDGE,"E43.0")])],"isStart":true})]});}
            var sketch = newSketch(context, id + "F21", { "sketchPlane" : qUnion([Q0])});
            skLineSegment(sketch, "E73", {"start": v(0, 0) * mm, "end": v(28.58, 0) * mm});
            skCircle(sketch, "E74", {"center": v(0, 57) * mm, "radius": 24 * mm});
            skCircle(sketch, "E75", {"center": v(0, 57) * mm, "radius": 32 * mm});
            skSolve(sketch);
        }
        {
            var Q0;
            Q0=makeQuery(id+"F21.imprint","IMPRINT",FACE,{"disambiguationData":[TD([[makeQuery(id+"F21.imprint","IMPRINT",EDGE,{"derivedFrom":sQuery(id+"F21.wireOp",EDGE,"E74")}),-1.0]])]});
            var Q1;
            {var subQ0=sQuery(id+"F6.wireOp",EDGE,"E14");var subQ1=sQuery(id+"F6.wireOp",EDGE,"E10");var subQ2=sQuery(id+"F6.wireOp",EDGE,"E8");Q1=makeQuery(id+"F21.imprint","IMPRINT",FACE,{"disambiguationData":[TD([[makeQuery(id+"F21.imprint","IMPRINT",EDGE,{"derivedFrom":makeQuery(id+"FJsTlNQASo6gJj2_17.opBoolean","INTERSECT",EDGE,{"derivedFrom":[makeQuery(id+"F11.boolean.opBoolean","MERGE",FACE,{"derivedFrom":[makeQuery(id+"FP5FcsPlQxCtVq2_5.opBoolean","MERGE",FACE,{"derivedFrom":[makeQuery(id+"F8.opRevolve","CAP_FACE",FACE,{"disambiguationData":[OSD([subQ2,subQ1,subQ0,sQuery(id+"F6.wireOp",EDGE,"E18"),sQuery(id+"F6.wireOp",EDGE,"E19"),sQuery(id+"F6.wireOp",EDGE,"E20"),sQuery(id+"F6.wireOp",EDGE,"E21"),sQuery(id+"F6.wireOp",EDGE,"E23")])],"isStart":false}),makeQuery(id+"F9.opRevolve","CAP_FACE",FACE,{"disambiguationData":[OSD([subQ2,subQ1,sQuery(id+"F6.wireOp",EDGE,"E11"),sQuery(id+"F6.wireOp",EDGE,"E12"),sQuery(id+"F6.wireOp",EDGE,"E13"),subQ0,sQuery(id+"F6.wireOp",EDGE,"E17"),sQuery(id+"F6.wireOp",EDGE,"E22")])],"isStart":false})]}),makeQuery(id+"F11.opRevolve","CAP_FACE",FACE,{"disambiguationData":[OSD([sQuery(id+"F10.wireOp",EDGE,"E43.0")])],"isStart":true})]}),makeQuery(id+"F19.opRevolve","SWEPT_FACE",FACE,{"disambiguationData":[OSD([sQuery(id+"F18.wireOp",EDGE,"E71")])]})]})}),-1.0]])]});}
            var Q2;
            {var subQ0=sQuery(id+"F6.wireOp",EDGE,"E14");var subQ1=sQuery(id+"F6.wireOp",EDGE,"E10");var subQ2=sQuery(id+"F6.wireOp",EDGE,"E8");Q2=makeQuery(id+"F21.imprint","IMPRINT",FACE,{"disambiguationData":[TD([[makeQuery(id+"F21.imprint","IMPRINT",EDGE,{"derivedFrom":makeQuery(id+"FJsTlNQASo6gJj2_17.opBoolean","INTERSECT",EDGE,{"derivedFrom":[makeQuery(id+"F11.boolean.opBoolean","MERGE",FACE,{"derivedFrom":[makeQuery(id+"FP5FcsPlQxCtVq2_5.opBoolean","MERGE",FACE,{"derivedFrom":[makeQuery(id+"F8.opRevolve","CAP_FACE",FACE,{"disambiguationData":[OSD([subQ2,subQ1,subQ0,sQuery(id+"F6.wireOp",EDGE,"E18"),sQuery(id+"F6.wireOp",EDGE,"E19"),sQuery(id+"F6.wireOp",EDGE,"E20"),sQuery(id+"F6.wireOp",EDGE,"E21"),sQuery(id+"F6.wireOp",EDGE,"E23")])],"isStart":false}),makeQuery(id+"F9.opRevolve","CAP_FACE",FACE,{"disambiguationData":[OSD([subQ2,subQ1,sQuery(id+"F6.wireOp",EDGE,"E11"),sQuery(id+"F6.wireOp",EDGE,"E12"),sQuery(id+"F6.wireOp",EDGE,"E13"),subQ0,sQuery(id+"F6.wireOp",EDGE,"E17"),sQuery(id+"F6.wireOp",EDGE,"E22")])],"isStart":false})]}),makeQuery(id+"F11.opRevolve","CAP_FACE",FACE,{"disambiguationData":[OSD([sQuery(id+"F10.wireOp",EDGE,"E43.0")])],"isStart":true})]}),makeQuery(id+"F19.opRevolve","SWEPT_FACE",FACE,{"disambiguationData":[OSD([sQuery(id+"F18.wireOp",EDGE,"E70")])]})]})}),-1.0]])]});}
            var Q3;
            {var subQ0=sQuery(id+"F6.wireOp",EDGE,"E14");var subQ1=sQuery(id+"F6.wireOp",EDGE,"E10");var subQ2=sQuery(id+"F6.wireOp",EDGE,"E8");Q3=makeQuery(id+"F21.imprint","IMPRINT",FACE,{"disambiguationData":[TD([[makeQuery(id+"F21.imprint","IMPRINT",EDGE,{"derivedFrom":makeQuery(id+"FJsTlNQASo6gJj2_17.opBoolean","INTERSECT",EDGE,{"derivedFrom":[makeQuery(id+"F11.boolean.opBoolean","MERGE",FACE,{"derivedFrom":[makeQuery(id+"FP5FcsPlQxCtVq2_5.opBoolean","MERGE",FACE,{"derivedFrom":[makeQuery(id+"F8.opRevolve","CAP_FACE",FACE,{"disambiguationData":[OSD([subQ2,subQ1,subQ0,sQuery(id+"F6.wireOp",EDGE,"E18"),sQuery(id+"F6.wireOp",EDGE,"E19"),sQuery(id+"F6.wireOp",EDGE,"E20"),sQuery(id+"F6.wireOp",EDGE,"E21"),sQuery(id+"F6.wireOp",EDGE,"E23")])],"isStart":false}),makeQuery(id+"F9.opRevolve","CAP_FACE",FACE,{"disambiguationData":[OSD([subQ2,subQ1,sQuery(id+"F6.wireOp",EDGE,"E11"),sQuery(id+"F6.wireOp",EDGE,"E12"),sQuery(id+"F6.wireOp",EDGE,"E13"),subQ0,sQuery(id+"F6.wireOp",EDGE,"E17"),sQuery(id+"F6.wireOp",EDGE,"E22")])],"isStart":false})]}),makeQuery(id+"F11.opRevolve","CAP_FACE",FACE,{"disambiguationData":[OSD([sQuery(id+"F10.wireOp",EDGE,"E43.0")])],"isStart":true})]}),makeQuery(id+"F19.opRevolve","SWEPT_FACE",FACE,{"disambiguationData":[OSD([sQuery(id+"F18.wireOp",EDGE,"E69")])]})]})}),-1.0]])]});}
            var Q4;
            {var subQ0=sQuery(id+"F6.wireOp",EDGE,"E14");var subQ1=sQuery(id+"F6.wireOp",EDGE,"E10");var subQ2=sQuery(id+"F6.wireOp",EDGE,"E8");Q4=makeQuery(id+"F21.imprint","IMPRINT",FACE,{"disambiguationData":[TD([[makeQuery(id+"F21.imprint","IMPRINT",EDGE,{"derivedFrom":makeQuery(id+"FJsTlNQASo6gJj2_17.opBoolean","INTERSECT",EDGE,{"derivedFrom":[makeQuery(id+"F11.boolean.opBoolean","MERGE",FACE,{"derivedFrom":[makeQuery(id+"FP5FcsPlQxCtVq2_5.opBoolean","MERGE",FACE,{"derivedFrom":[makeQuery(id+"F8.opRevolve","CAP_FACE",FACE,{"disambiguationData":[OSD([subQ2,subQ1,subQ0,sQuery(id+"F6.wireOp",EDGE,"E18"),sQuery(id+"F6.wireOp",EDGE,"E19"),sQuery(id+"F6.wireOp",EDGE,"E20"),sQuery(id+"F6.wireOp",EDGE,"E21"),sQuery(id+"F6.wireOp",EDGE,"E23")])],"isStart":false}),makeQuery(id+"F9.opRevolve","CAP_FACE",FACE,{"disambiguationData":[OSD([subQ2,subQ1,sQuery(id+"F6.wireOp",EDGE,"E11"),sQuery(id+"F6.wireOp",EDGE,"E12"),sQuery(id+"F6.wireOp",EDGE,"E13"),subQ0,sQuery(id+"F6.wireOp",EDGE,"E17"),sQuery(id+"F6.wireOp",EDGE,"E22")])],"isStart":false})]}),makeQuery(id+"F11.opRevolve","CAP_FACE",FACE,{"disambiguationData":[OSD([sQuery(id+"F10.wireOp",EDGE,"E43.0")])],"isStart":true})]}),makeQuery(id+"F19.opRevolve","SWEPT_FACE",FACE,{"disambiguationData":[OSD([sQuery(id+"F18.wireOp",EDGE,"E67")])]})]})}),-1.0]])]});}
            var Q5;
            {var subQ0=sQuery(id+"F6.wireOp",EDGE,"E14");var subQ1=sQuery(id+"F6.wireOp",EDGE,"E10");var subQ2=sQuery(id+"F6.wireOp",EDGE,"E8");Q5=makeQuery(id+"F21.imprint","IMPRINT",FACE,{"disambiguationData":[TD([[makeQuery(id+"F21.imprint","IMPRINT",EDGE,{"derivedFrom":makeQuery(id+"FJsTlNQASo6gJj2_17.opBoolean","INTERSECT",EDGE,{"derivedFrom":[makeQuery(id+"F11.boolean.opBoolean","MERGE",FACE,{"derivedFrom":[makeQuery(id+"FP5FcsPlQxCtVq2_5.opBoolean","MERGE",FACE,{"derivedFrom":[makeQuery(id+"F8.opRevolve","CAP_FACE",FACE,{"disambiguationData":[OSD([subQ2,subQ1,subQ0,sQuery(id+"F6.wireOp",EDGE,"E18"),sQuery(id+"F6.wireOp",EDGE,"E19"),sQuery(id+"F6.wireOp",EDGE,"E20"),sQuery(id+"F6.wireOp",EDGE,"E21"),sQuery(id+"F6.wireOp",EDGE,"E23")])],"isStart":false}),makeQuery(id+"F9.opRevolve","CAP_FACE",FACE,{"disambiguationData":[OSD([subQ2,subQ1,sQuery(id+"F6.wireOp",EDGE,"E11"),sQuery(id+"F6.wireOp",EDGE,"E12"),sQuery(id+"F6.wireOp",EDGE,"E13"),subQ0,sQuery(id+"F6.wireOp",EDGE,"E17"),sQuery(id+"F6.wireOp",EDGE,"E22")])],"isStart":false})]}),makeQuery(id+"F11.opRevolve","CAP_FACE",FACE,{"disambiguationData":[OSD([sQuery(id+"F10.wireOp",EDGE,"E43.0")])],"isStart":true})]}),makeQuery(id+"F19.opRevolve","SWEPT_FACE",FACE,{"disambiguationData":[OSD([sQuery(id+"F18.wireOp",EDGE,"E68")])]})]})}),-1.0]])]});}
            var Q6;
            {var subQ0=sQuery(id+"F6.wireOp",EDGE,"E14");var subQ1=sQuery(id+"F6.wireOp",EDGE,"E10");var subQ2=sQuery(id+"F6.wireOp",EDGE,"E8");Q6=makeQuery(id+"F21.imprint","IMPRINT",FACE,{"disambiguationData":[TD([[makeQuery(id+"F21.imprint","IMPRINT",EDGE,{"derivedFrom":makeQuery(id+"FJsTlNQASo6gJj2_17.opBoolean","INTERSECT",EDGE,{"derivedFrom":[makeQuery(id+"F11.boolean.opBoolean","MERGE",FACE,{"derivedFrom":[makeQuery(id+"FP5FcsPlQxCtVq2_5.opBoolean","MERGE",FACE,{"derivedFrom":[makeQuery(id+"F8.opRevolve","CAP_FACE",FACE,{"disambiguationData":[OSD([subQ2,subQ1,subQ0,sQuery(id+"F6.wireOp",EDGE,"E18"),sQuery(id+"F6.wireOp",EDGE,"E19"),sQuery(id+"F6.wireOp",EDGE,"E20"),sQuery(id+"F6.wireOp",EDGE,"E21"),sQuery(id+"F6.wireOp",EDGE,"E23")])],"isStart":false}),makeQuery(id+"F9.opRevolve","CAP_FACE",FACE,{"disambiguationData":[OSD([subQ2,subQ1,sQuery(id+"F6.wireOp",EDGE,"E11"),sQuery(id+"F6.wireOp",EDGE,"E12"),sQuery(id+"F6.wireOp",EDGE,"E13"),subQ0,sQuery(id+"F6.wireOp",EDGE,"E17"),sQuery(id+"F6.wireOp",EDGE,"E22")])],"isStart":false})]}),makeQuery(id+"F11.opRevolve","CAP_FACE",FACE,{"disambiguationData":[OSD([sQuery(id+"F10.wireOp",EDGE,"E43.0")])],"isStart":true})]}),makeQuery(id+"F19.opRevolve","SWEPT_FACE",FACE,{"disambiguationData":[OSD([sQuery(id+"F18.wireOp",EDGE,"E72")])]})]})}),-1.0]])]});}
            var Q7;
            Q7=sQuery(id+"F21.wireOp",EDGE,"E73");
            revolve(context, id + "F22", {"entities" : qUnion([Q0, Q1, Q2, Q3, Q4, Q5, Q6]), "axis" : qUnion([Q7]), "revolveType" : RevolveType.SYMMETRIC, "oppositeDirection" : true, "angle" : 8 * degree});
        }
        {
            var Q0;
            Q0=qCreatedBy(makeId("Front.planeOp"),FACE);
            var sketch = newSketch(context, id + "F23", { "sketchPlane" : qUnion([Q0])});
            skLineSegment(sketch, "E76.bottom", {"start": v(0, 0) * mm, "end": v(400, 0) * mm});
            skLineSegment(sketch, "E76.top", {"start": v(0, 45) * mm, "end": v(400, 45) * mm});
            skLineSegment(sketch, "E76.left", {"start": v(0, 0) * mm, "end": v(0, 45) * mm});
            skLineSegment(sketch, "E76.right", {"start": v(400, 0) * mm, "end": v(400, 45) * mm});
            skLineSegment(sketch, "E77", {"start": v(0, 0) * mm, "end": v(-55.01, 0) * mm, "construction": true});
            skLineSegment(sketch, "E78", {"start": v(0, 35) * mm, "end": v(50, 35) * mm});
            skLineSegment(sketch, "E79", {"start": v(50, 35) * mm, "end": v(99.28, 12.5) * mm});
            skLineSegment(sketch, "E80", {"start": v(99.28, 12.5) * mm, "end": v(199.28, 12.5) * mm});
            skLineSegment(sketch, "E81", {"start": v(199.28, 12.5) * mm, "end": v(260, 40) * mm});
            skLineSegment(sketch, "E82", {"start": v(260, 40) * mm, "end": v(400, 40) * mm});
            skSolve(sketch);
        }
        {
            var Q0;
            {var subQ2=sQuery(id+"F23.wireOp",EDGE,"E76.top");Q0=makeQuery(id+"F23.imprint","IMPRINT",FACE,{"disambiguationData":[TD([[makeQuery(id+"F23.imprint","IMPRINT",EDGE,{"derivedFrom":subQ2}),-1.0]])]});}
            var Q1;
            Q1=sQuery(id+"F23.wireOp",EDGE,"E77");
            revolve(context, id + "F24", {"entities" : qUnion([Q0]), "axis" : qUnion([Q1]), "revolveType" : RevolveType.FULL});
        }
        {
            var Q0;
            Q0=qCreatedBy(makeId("Right.planeOp"),FACE);
            var sketch = newSketch(context, id + "F25", { "sketchPlane" : qUnion([Q0])});
            skCircle(sketch, "E83", {"center": v(-55.84, 76.86) * mm, "radius": 4.1 * mm});
            skLineSegment(sketch, "E84", {"start": v(0, 115.78) * mm, "end": v(0, 0) * mm, "construction": true});
            skLineSegment(sketch, "E85", {"start": v(0, 0) * mm, "end": v(-55.84, 76.86) * mm, "construction": true});
            skCircle(sketch, "E86", {"center": v(-29.36, 90.35) * mm, "radius": 4.1 * mm});
            skLineSegment(sketch, "E87", {"start": v(0, 0) * mm, "end": v(-29.36, 90.35) * mm, "construction": true});
            skCircle(sketch, "E88", {"center": v(0, 95) * mm, "radius": 4.1 * mm});
            skCircle(sketch, "E89.MirrorC", {"center": v(29.36, 90.35) * mm, "radius": 4.1 * mm});
            skCircle(sketch, "E90.MirrorC", {"center": v(55.84, 76.86) * mm, "radius": 4.1 * mm});
            skSolve(sketch);
        }
        {
            var Q0;
            Q0 = qSketchRegion(id + "F25", true);
            extrude(context, id + "F26", {"entities" : qUnion([Q0]), "endBound" : BoundingType.SYMMETRIC, "oppositeDirection" : true, "depth" : 100 * mm});
        }
        {
            var Q0;
            Q0=qCreatedBy(makeId("Right.planeOp"),FACE);
            var sketch = newSketch(context, id + "F27", { "sketchPlane" : qUnion([Q0])});
            skCircle(sketch, "E91", {"center": v(9.23, 25.37) * mm, "radius": 4.1 * mm});
            skLineSegment(sketch, "E92", {"start": v(0, 0) * mm, "end": v(9.23, 25.37) * mm, "construction": true});
            skLineSegment(sketch, "E93", {"start": v(0, 0) * mm, "end": v(0, -100.87) * mm, "construction": true});
            skCircle(sketch, "E94.MirrorC", {"center": v(-9.23, 25.37) * mm, "radius": 4.1 * mm});
            skSolve(sketch);
        }
        {
            var Q0;
            Q0 = qSketchRegion(id + "F27", true);
            extrude(context, id + "F28", {"entities" : qUnion([Q0]), "endBound" : BoundingType.SYMMETRIC, "depth" : 100 * mm});
        }
        {
            var Q0;
            Q0=makeQuery(id+"F26.opExtrude","SWEPT_BODY",BODY,{"disambiguationData":[OSD([sQuery(id+"F25.wireOp",EDGE,"E83")])]});
            var Q1;
            Q1=makeQuery(id+"F26.opExtrude","SWEPT_BODY",BODY,{"disambiguationData":[OSD([sQuery(id+"F25.wireOp",EDGE,"E86")])]});
            var Q2;
            Q2=makeQuery(id+"F26.opExtrude","SWEPT_BODY",BODY,{"disambiguationData":[OSD([sQuery(id+"F25.wireOp",EDGE,"E88")])]});
            var Q3;
            Q3=makeQuery(id+"F26.opExtrude","SWEPT_BODY",BODY,{"disambiguationData":[OSD([sQuery(id+"F25.wireOp",EDGE,"E89.MirrorC")])]});
            var Q4;
            Q4=makeQuery(id+"F26.opExtrude","SWEPT_BODY",BODY,{"disambiguationData":[OSD([sQuery(id+"F25.wireOp",EDGE,"E90.MirrorC")])]});
            var Q5;
            Q5=makeQuery(id+"F28.opExtrude","SWEPT_BODY",BODY,{"disambiguationData":[OSD([sQuery(id+"F27.wireOp",EDGE,"E91")])]});
            var Q6;
            Q6=makeQuery(id+"F28.opExtrude","SWEPT_BODY",BODY,{"disambiguationData":[OSD([sQuery(id+"F27.wireOp",EDGE,"E94.MirrorC")])]});
            var Q7;
            Q7=makeQuery(id+"F9.opRevolve","SWEPT_BODY",BODY,{"disambiguationData":[OSD([sQuery(id+"F6.wireOp",EDGE,"E8"),sQuery(id+"F6.wireOp",EDGE,"E10"),sQuery(id+"F6.wireOp",EDGE,"E11"),sQuery(id+"F6.wireOp",EDGE,"E12"),sQuery(id+"F6.wireOp",EDGE,"E13"),sQuery(id+"F6.wireOp",EDGE,"E14"),sQuery(id+"F6.wireOp",EDGE,"E17"),sQuery(id+"F6.wireOp",EDGE,"E22")])]});
            var Q8;
            Q8=makeQuery(id+"F8.opRevolve","SWEPT_BODY",BODY,{"disambiguationData":[OSD([sQuery(id+"F6.wireOp",EDGE,"E8"),sQuery(id+"F6.wireOp",EDGE,"E10"),sQuery(id+"F6.wireOp",EDGE,"E14"),sQuery(id+"F6.wireOp",EDGE,"E18"),sQuery(id+"F6.wireOp",EDGE,"E19"),sQuery(id+"F6.wireOp",EDGE,"E20"),sQuery(id+"F6.wireOp",EDGE,"E21"),sQuery(id+"F6.wireOp",EDGE,"E23")])]});
            booleanBodies(context, id + "F29", {"operationType" : BooleanOperationType.SUBTRACTION, "tools" : qUnion([Q0, Q1, Q2, Q3, Q4, Q5, Q6]), "targets" : qUnion([Q7, Q8])});
        }
        {
            var Q0;
            Q0=makeQuery(id+"F8.opRevolve","SWEPT_FACE",FACE,{"disambiguationData":[OSD([sQuery(id+"F6.wireOp",EDGE,"E19")])]});
            shell(context, id + "F30", {"entities" : qUnion([Q0]), "thickness" : 8 * mm});
        }
        {
            var Q0;
            Q0=makeQuery(id+"F9.opRevolve","SWEPT_FACE",FACE,{"disambiguationData":[OSD([sQuery(id+"F6.wireOp",EDGE,"E12")])]});
            shell(context, id + "F31", {"entities" : qUnion([Q0]), "thickness" : 8 * mm});
        }
        {
            var Q0;
            Q0=makeQuery(id+"F1.opExtrude","SWEPT_BODY",BODY,{"disambiguationData":[OSD([sQuery(id+"F0.wireOp",EDGE,"E0.bottom"),sQuery(id+"F0.wireOp",EDGE,"E0.top"),sQuery(id+"F0.wireOp",EDGE,"E0.left"),sQuery(id+"F0.wireOp",EDGE,"E0.right"),sQuery(id+"F0.wireOp",EDGE,"E1"),sQuery(id+"F0.wireOp",EDGE,"E2"),sQuery(id+"F0.wireOp",EDGE,"E3"),sQuery(id+"F0.wireOp",EDGE,"E4")])]});
            var Q1;
            Q1=makeQuery(id+"F1.opExtrude","CAP_FACE",FACE,{"disambiguationData":[OSD([sQuery(id+"F0.wireOp",EDGE,"E0.bottom"),sQuery(id+"F0.wireOp",EDGE,"E0.top"),sQuery(id+"F0.wireOp",EDGE,"E0.left"),sQuery(id+"F0.wireOp",EDGE,"E0.right"),sQuery(id+"F0.wireOp",EDGE,"E1"),sQuery(id+"F0.wireOp",EDGE,"E2"),sQuery(id+"F0.wireOp",EDGE,"E3"),sQuery(id+"F0.wireOp",EDGE,"E4")])],"isStart":true});
            mirror(context, id + "F32", {"operationType" : NewBodyOperationType.ADD, "entities" : qUnion([Q0]), "mirrorPlane" : qUnion([Q1])});
        }
    });
